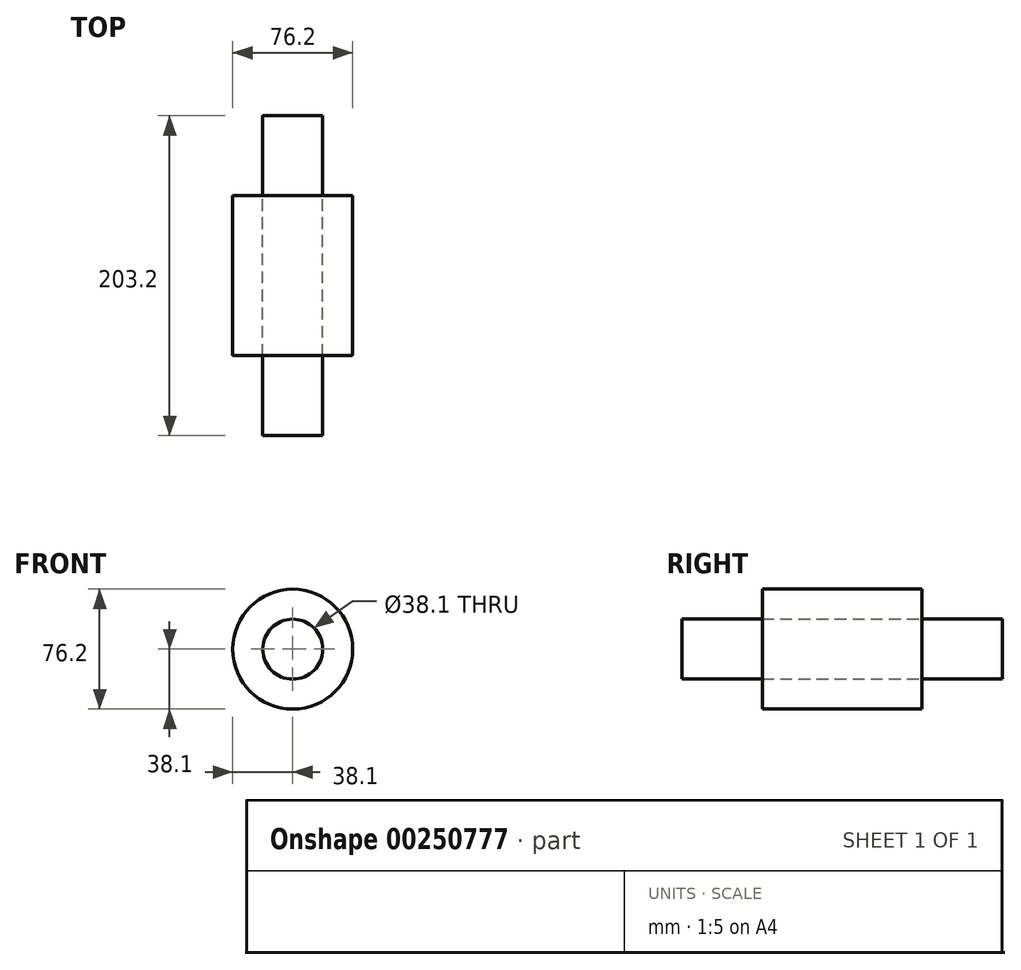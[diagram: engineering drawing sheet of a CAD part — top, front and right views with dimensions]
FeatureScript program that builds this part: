
annotation { "Feature Type Name" : "Feature", "Feature Type Description" : "" }
export const myFeature = defineFeature(function(context is Context, id is Id, definition is map)
    precondition{}
    {
        {
            var Q0;
            Q0=qCreatedBy(makeId("Front.planeOp"),FACE);
            var sketch = newSketch(context, id + "F0", { "sketchPlane" : qUnion([Q0])});
            skCircle(sketch, "E0", {"center": v(0, 0) * mm, "radius": 38.1 * mm});
            skCircle(sketch, "E1", {"center": v(0, 0) * mm, "radius": 19.05 * mm});
            skSolve(sketch);
        }
        {
            var Q0;
            Q0=makeQuery(id+"F0.imprint","IMPRINT",FACE,{"disambiguationData":[TD([[makeQuery(id+"F0.imprint","IMPRINT",EDGE,{"derivedFrom":sQuery(id+"F0.wireOp",EDGE,"E0")}),1.0]])]});
            extrude(context, id + "F1", {"entities" : qUnion([Q0]), "endBound" : BoundingType.SYMMETRIC, "oppositeDirection" : true, "depth" : 101.6 * mm});
        }
        {
            var Q0;
            Q0=makeQuery(id+"F0.imprint","IMPRINT",FACE,{"disambiguationData":[TD([[makeQuery(id+"F0.imprint","IMPRINT",EDGE,{"derivedFrom":sQuery(id+"F0.wireOp",EDGE,"E1")}),1.0]])]});
            extrude(context, id + "F2", {"entities" : qUnion([Q0]), "endBound" : BoundingType.SYMMETRIC, "depth" : 203.2 * mm});
        }
    });
